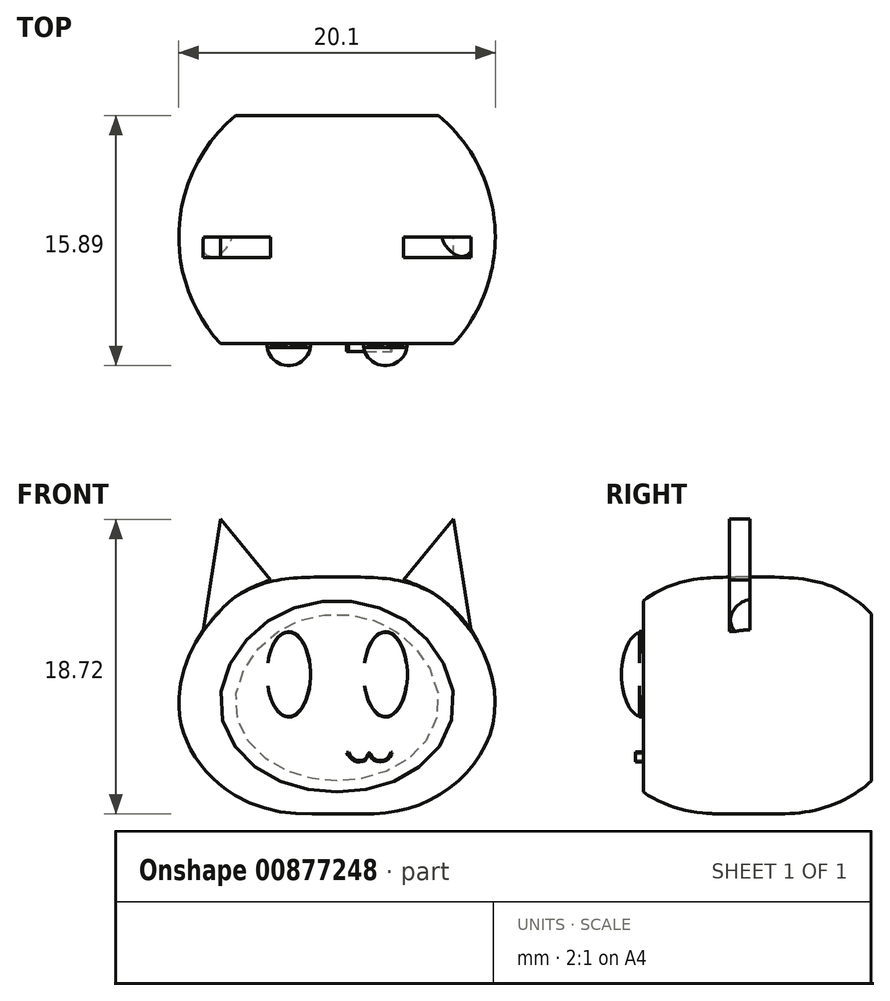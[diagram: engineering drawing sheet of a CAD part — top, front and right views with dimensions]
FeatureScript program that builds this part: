
annotation { "Feature Type Name" : "Feature", "Feature Type Description" : "" }
export const myFeature = defineFeature(function(context is Context, id is Id, definition is map)
    precondition{}
    {
        {
            var Q0;
            Q0=qCreatedBy(makeId("Front.planeOp"),FACE);
            var sketch = newSketch(context, id + "F0", { "sketchPlane" : qUnion([Q0])});
            skFitSpline(sketch, "E0", {"points": [v(0, 23.28) * mm, v(4.7, 22.87) * mm, v(8.11, 20.46) * mm, v(9.98, 16.22) * mm, v(9.48, 12.73) * mm, v(7.28, 9.99) * mm, v(3.96, 8.45) * mm, v(0, 8.28) * mm], "startDerivative": vector(31.74, 0.32) * mm, "endDerivative": vector(-28.45, 1) * mm});
            skLineSegment(sketch, "E1", {"start": v(0, 23.28) * mm, "end": v(0, 8.28) * mm});
            skSolve(sketch);
        }
        {
            var Q0;
            Q0=makeQuery(id+"F0.imprint","IMPRINT",FACE,{"disambiguationData":[TD([[makeQuery(id+"F0.imprint","IMPRINT",EDGE,{"derivedFrom":sQuery(id+"F0.wireOp",EDGE,"E0")}),-1.0]])]});
            var Q1;
            Q1=sQuery(id+"F0.wireOp",EDGE,"E1");
            revolve(context, id + "F1", {"surfaceOperationType" : NewSurfaceOperationType.NEW, "entities" : qUnion([Q0]), "axis" : qUnion([Q1]), "revolveType" : RevolveType.FULL});
        }
        {
            var Q0;
            Q0=qCreatedBy(makeId("Front.planeOp"),FACE);
            var sketch = newSketch(context, id + "F2", { "sketchPlane" : qUnion([Q0])});
            skLineSegment(sketch, "E2", {"start": v(4.22, 23.11) * mm, "end": v(7.4, 26.96) * mm});
            skLineSegment(sketch, "E3", {"start": v(7.4, 26.96) * mm, "end": v(8.5, 19.84) * mm});
            skFitSpline(sketch, "E4", {"points": [v(4.22, 23.11) * mm, v(6.49, 22) * mm, v(8.5, 19.84) * mm], "startDerivative": vector(4.92, -1.86) * mm, "endDerivative": vector(3.67, -4.65) * mm});
            skSolve(sketch);
        }
        {
            var Q0;
            Q0=makeQuery(id+"F2.imprint","IMPRINT",FACE,{"disambiguationData":[TD([[makeQuery(id+"F2.imprint","IMPRINT",EDGE,{"derivedFrom":sQuery(id+"F2.wireOp",EDGE,"E2")}),-1.0]])]});
            extrude(context, id + "F3", {"entities" : qUnion([Q0]), "operationType" : NewBodyOperationType.ADD, "depth" : 1.3 * mm, "offsetDistance" : 25 * mm});
        }
        {
            var Q0;
            Q0=makeQuery(id+"F1.opRevolve","SWEPT_BODY",BODY,{"disambiguationData":[OSD([sQuery(id+"F0.wireOp",EDGE,"E0"),sQuery(id+"F0.wireOp",EDGE,"E1")])]});
            var Q1;
            Q1=qCreatedBy(makeId("Right.planeOp"),FACE);
            mirror(context, id + "F4", {"operationType" : NewBodyOperationType.ADD, "entities" : qUnion([Q0]), "mirrorPlane" : qUnion([Q1])});
        }
        {
            var Q0;
            Q0=qCreatedBy(makeId("Right.planeOp"),FACE);
            var sketch = newSketch(context, id + "F5", { "sketchPlane" : qUnion([Q0])});
            skPoint(sketch, "E5", {"position": v(0, 16.43) * mm});
            skPoint(sketch, "E6", {"position": v(26.21, 16.43) * mm});
            skLineSegment(sketch, "E7", {"start": v(0, 16.43) * mm, "end": v(26.21, 16.43) * mm});
            skSolve(sketch);
        }
        {
            var Q0;
            Q0=makeQuery(id+"F1.opRevolve","SWEPT_BODY",BODY,{"disambiguationData":[OSD([sQuery(id+"F0.wireOp",EDGE,"E0"),sQuery(id+"F0.wireOp",EDGE,"E1")])]});
            var Q1;
            Q1=sQuery(id+"F5.wireOp",EDGE,"E7");
            transform(context, id + "F6", {"entities" : qUnion([Q0]), "transformType" : TransformType.TRANSLATION_ENTITY, "oppositeDirectionEntity" : false, "transformLine" : qUnion([Q1]), "makeCopy" : false});
        }
        {
            var Q0;
            Q0=qCreatedBy(makeId("Right.planeOp"),FACE);
            var sketch = newSketch(context, id + "F7", { "sketchPlane" : qUnion([Q0])});
            skPoint(sketch, "E8", {"position": v(17.4, 15.52) * mm});
            skPoint(sketch, "E9", {"position": v(-2.02, 15.78) * mm});
            skLineSegment(sketch, "E10", {"start": v(17.4, 15.52) * mm, "end": v(-2.02, 15.78) * mm});
            skSolve(sketch);
        }
        {
            var Q0;
            Q0=makeQuery(id+"F1.opRevolve","SWEPT_BODY",BODY,{"disambiguationData":[OSD([sQuery(id+"F0.wireOp",EDGE,"E0"),sQuery(id+"F0.wireOp",EDGE,"E1")])]});
            var Q1;
            Q1=sQuery(id+"F7.wireOp",EDGE,"E10");
            transform(context, id + "F8", {"entities" : qUnion([Q0]), "transformType" : TransformType.TRANSLATION_ENTITY, "oppositeDirectionEntity" : false, "transformLine" : qUnion([Q1]), "makeCopy" : false});
        }
        {
            var Q0;
            Q0=qCreatedBy(makeId("Front.planeOp"),FACE);
            var sketch = newSketch(context, id + "F9", { "sketchPlane" : qUnion([Q0])});
            skEllipse(sketch, "E11", {"center": v(-20.08, 20.47) * mm, "majorRadius": 2.72 * mm, "minorRadius": 1.37 * mm, "majorAxis": v(0, -1)});
            skSolve(sketch);
        }
        {
            var Q0;
            Q0=makeQuery(id+"F9.imprint","IMPRINT",FACE,{"disambiguationData":[TD([[makeQuery(id+"F9.imprint","IMPRINT",EDGE,{"derivedFrom":sQuery(id+"F9.wireOp",EDGE,"E11")}),1.0]])]});
            extrude(context, id + "F10", {"entities" : qUnion([Q0]), "endBound" : BoundingType.SYMMETRIC, "depth" : 0.5 * mm, "offsetDistance" : 25 * mm});
        }
        {
            var Q0;
            Q0=qCreatedBy(makeId("Front.planeOp"),FACE);
            var sketch = newSketch(context, id + "F11", { "sketchPlane" : qUnion([Q0])});
            skLineSegment(sketch, "E12.bottom", {"start": v(-10.93, 24.87) * mm, "end": v(11.9, 24.87) * mm});
            skLineSegment(sketch, "E12.top", {"start": v(-10.93, 6.34) * mm, "end": v(11.9, 6.34) * mm});
            skLineSegment(sketch, "E12.left", {"start": v(-10.93, 24.87) * mm, "end": v(-10.93, 6.34) * mm});
            skLineSegment(sketch, "E12.right", {"start": v(11.9, 24.87) * mm, "end": v(11.9, 6.34) * mm});
            skSolve(sketch);
        }
        {
            var Q0;
            Q0 = qSketchRegion(id + "F11", true);
            extrude(context, id + "F12", {"entities" : qUnion([Q0]), "operationType" : NewBodyOperationType.REMOVE, "depth" : 10.7 * mm, "offsetDistance" : 25 * mm});
        }
        {
            var Q0;
            Q0=qCreatedBy(makeId("Front.planeOp"),FACE);
            var sketch = newSketch(context, id + "F13", { "sketchPlane" : qUnion([Q0])});
            skPoint(sketch, "E13", {"position": v(-20.4, 20.98) * mm});
            skPoint(sketch, "E14", {"position": v(-3.39, 17.88) * mm});
            skLineSegment(sketch, "E15", {"start": v(-20.4, 20.98) * mm, "end": v(-3.39, 17.88) * mm});
            skSolve(sketch);
        }
        {
            var Q0;
            Q0=makeQuery(id+"F10.opExtrude","SWEPT_BODY",BODY,{"disambiguationData":[OSD([sQuery(id+"F9.wireOp",EDGE,"E11")])]});
            var Q1;
            Q1=sQuery(id+"F13.wireOp",EDGE,"E15");
            transform(context, id + "F14", {"entities" : qUnion([Q0]), "transformType" : TransformType.TRANSLATION_ENTITY, "oppositeDirectionEntity" : false, "transformLine" : qUnion([Q1]), "makeCopy" : false});
        }
        {
            var Q0;
            Q0=makeQuery(id+"F10.opExtrude","SWEPT_BODY",BODY,{"disambiguationData":[OSD([sQuery(id+"F9.wireOp",EDGE,"E11")])]});
            var Q1;
            Q1=qCreatedBy(makeId("Right.planeOp"),FACE);
            mirror(context, id + "F15", {"operationType" : NewBodyOperationType.ADD, "entities" : qUnion([Q0]), "mirrorPlane" : qUnion([Q1])});
        }
        {
            var Q0;
            Q0=qCreatedBy(makeId("Front.planeOp"),FACE);
            var sketch = newSketch(context, id + "F16", { "sketchPlane" : qUnion([Q0])});
            skFitSpline(sketch, "E16.0.0", {"points": [v(-1.1, 9.93) * mm, v(0, 9.86) * mm, v(1.11, 9.93) * mm, v(1.99, 10.08) * mm, v(2.84, 10.28) * mm, v(3.67, 10.58) * mm, v(4.46, 11) * mm, v(5.02, 11.34) * mm, v(5.54, 11.75) * mm, v(6.03, 12.21) * mm, v(6.46, 12.72) * mm, v(6.82, 13.28) * mm, v(7.1, 13.88) * mm, v(7.3, 14.51) * mm, v(7.41, 15.18) * mm, v(7.42, 15.84) * mm, v(7.33, 16.5) * mm, v(7.16, 17.15) * mm, v(6.92, 17.76) * mm, v(6.61, 18.36) * mm, v(6.25, 18.92) * mm, v(5.85, 19.44) * mm, v(5.4, 19.93) * mm, v(4.9, 20.38) * mm, v(4.38, 20.77) * mm, v(3.82, 21.11) * mm, v(3.23, 21.4) * mm, v(2.6, 21.64) * mm, v(1.96, 21.82) * mm, v(1.31, 21.94) * mm, v(0.66, 22.02) * mm, v(0, 22.04) * mm, v(-0.67, 22.01) * mm, v(-1.33, 21.94) * mm, v(-1.98, 21.81) * mm, v(-2.62, 21.63) * mm, v(-3.24, 21.4) * mm, v(-3.83, 21.1) * mm, v(-4.4, 20.76) * mm, v(-5.1, 20.22) * mm, v(-5.73, 19.6) * mm, v(-6.27, 18.9) * mm, v(-6.63, 18.33) * mm, v(-6.92, 17.75) * mm, v(-7.16, 17.13) * mm, v(-7.33, 16.48) * mm, v(-7.42, 15.82) * mm, v(-7.4, 15.15) * mm, v(-7.3, 14.5) * mm, v(-7.1, 13.87) * mm, v(-6.81, 13.26) * mm, v(-6.45, 12.71) * mm, v(-6.02, 12.2) * mm, v(-5.54, 11.74) * mm, v(-4.84, 11.2) * mm, v(-3.87, 10.65) * mm, v(-2.84, 10.28) * mm, v(-1.98, 10.08) * mm, v(-1.1, 9.93) * mm, v(0, 9.86) * mm, v(1.11, 9.93) * mm, v(-1.1, 9.93) * mm]});
            skFitSpline(sketch, "E17", {"points": [v(0.74, 12.4) * mm, v(1.17, 11.94) * mm, v(1.81, 12.04) * mm, v(2.04, 12.4) * mm, v(2.32, 12) * mm, v(3.14, 12) * mm, v(3.41, 12.43) * mm], "startDerivative": vector(1.98, -3.24) * mm, "endDerivative": vector(1.03, 3.1) * mm});
            skFitSpline(sketch, "E18", {"points": [v(0.6, 12.4) * mm, v(1.12, 11.85) * mm, v(1.85, 11.97) * mm, v(2.04, 12.3) * mm, v(2.29, 11.94) * mm, v(3.17, 11.91) * mm, v(3.5, 12.42) * mm], "startDerivative": vector(2.28, -3.73) * mm, "endDerivative": vector(1.18, 3.6) * mm});
            skLineSegment(sketch, "E19", {"start": v(0.74, 12.4) * mm, "end": v(0.6, 12.4) * mm});
            skLineSegment(sketch, "E20", {"start": v(3.5, 12.42) * mm, "end": v(3.41, 12.43) * mm});
            skSolve(sketch);
        }
        {
            var Q0;
            Q0=makeQuery(id+"F16.imprint","IMPRINT",FACE,{"disambiguationData":[TD([[makeQuery(id+"F16.imprint","IMPRINT",EDGE,{"derivedFrom":sQuery(id+"F16.wireOp",EDGE,"E17")}),-1.0]])]});
            extrude(context, id + "F17", {"entities" : qUnion([Q0]), "operationType" : NewBodyOperationType.ADD, "depth" : .5 * mm, "offsetDistance" : 25 * mm});
        }
        {
            var Q0;
            Q0=makeQuery(id+"F12.boolean.opBoolean","COPY",FACE,{"derivedFrom":makeQuery(id+"F12.opExtrude","CAP_FACE",FACE,{"disambiguationData":[OSD([sQuery(id+"F11.wireOp",EDGE,"E12.bottom"),sQuery(id+"F11.wireOp",EDGE,"E12.top"),sQuery(id+"F11.wireOp",EDGE,"E12.left"),sQuery(id+"F11.wireOp",EDGE,"E12.right")])],"isStart":true})});
            var sketch = newSketch(context, id + "F18", { "sketchPlane" : qUnion([Q0])});
            skLineSegment(sketch, "E21", {"start": v(3.07, 14.65) * mm, "end": v(3.07, 20.08) * mm});
            skEllipticalArc(sketch, "E22", {});
            const initialGuessF18  = {"E22": [0.0030728483106940985, 0.017364149913191795, 0, -1, 0.0027151592075824738, 0.0013951288416497846, 0, 3.141592653589793]};
            skSetInitialGuess(sketch, initialGuessF18);
            skSolve(sketch);
        }
        {
            var Q0;
            Q0 = qSketchRegion(id + "F18", true);
            var Q1;
            Q1=sQuery(id+"F18.wireOp",EDGE,"E21");
            revolve(context, id + "F19", {"surfaceOperationType" : NewSurfaceOperationType.NEW, "entities" : qUnion([Q0]), "axis" : qUnion([Q1]), "revolveType" : RevolveType.ONE_DIRECTION, "oppositeDirection" : true, "angle" : 180 * degree});
        }
        {
            var Q0;
            Q0=makeQuery(id+"F19.opRevolve","SWEPT_BODY",BODY,{"disambiguationData":[OSD([sQuery(id+"F18.wireOp",EDGE,"E22"),sQuery(id+"F18.wireOp",EDGE,"E21")])]});
            var Q1;
            Q1=qCreatedBy(makeId("Right.planeOp"),FACE);
            mirror(context, id + "F20", {"operationType" : NewBodyOperationType.ADD, "entities" : qUnion([Q0]), "mirrorPlane" : qUnion([Q1])});
        }
        {
            var Q0;
            Q0=qCreatedBy(makeId("Right.planeOp"),FACE);
            var sketch = newSketch(context, id + "F21", { "sketchPlane" : qUnion([Q0])});
            skLineSegment(sketch, "E23.bottom", {"start": v(14.49, 24.42) * mm, "end": v(21.68, 24.42) * mm});
            skLineSegment(sketch, "E23.top", {"start": v(14.49, 6.54) * mm, "end": v(21.68, 6.54) * mm});
            skLineSegment(sketch, "E23.left", {"start": v(14.49, 24.42) * mm, "end": v(14.49, 6.54) * mm});
            skLineSegment(sketch, "E23.right", {"start": v(21.68, 24.42) * mm, "end": v(21.68, 6.54) * mm});
            skSolve(sketch);
        }
        {
            var Q0;
            Q0=makeQuery(id+"F21.imprint","IMPRINT",FACE,{"disambiguationData":[TD([[makeQuery(id+"F21.imprint","IMPRINT",EDGE,{"derivedFrom":sQuery(id+"F21.wireOp",EDGE,"E23.bottom")}),-1.0]])]});
            extrude(context, id + "F22", {"entities" : qUnion([Q0]), "operationType" : NewBodyOperationType.REMOVE, "endBound" : BoundingType.SYMMETRIC, "oppositeDirection" : true, "depth" : 25 * mm, "offsetDistance" : 25 * mm});
        }
    });
